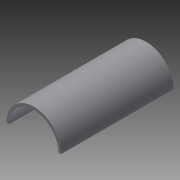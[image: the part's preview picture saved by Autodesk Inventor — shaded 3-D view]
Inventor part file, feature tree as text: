
AUTODESK INVENTOR PART (.ipt)
format: ipt  version: 2014 (Build 180170000, 170)  size: 78,848 bytes
history: native  units: mm
features: extrude x1, sketch x1
ambient origin geometry x8: Origin, YZ Plane, XZ Plane, XY Plane, X Axis, Y Axis, Z Axis, Center Point
bodies: Solid1 (feature_tree)
feature tree (2):
  extrude  "Extrusion1"  Depth=160.0mm
  sketch  "Sketch1"  dims[d0=70.0mm d1=78.0mm d2=160.0mm d3=0.0mm]
